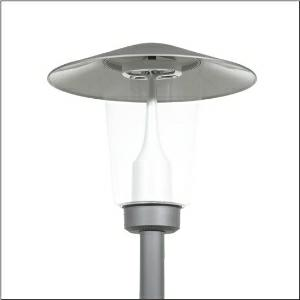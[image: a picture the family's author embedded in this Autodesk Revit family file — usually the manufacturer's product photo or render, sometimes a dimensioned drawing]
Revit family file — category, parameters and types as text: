
# Revit family: pilzleuchte_iq___p1_0a_5xa5235bf14hp_6096
name_source: partatom
category: Lighting Fixtures
units: mm (PartAtom-declared; Revit-internal decimal feet)

## family parameters
Cut with Voids When Loaded = No
Host = Face
Light Source = No
Part Type = Normal
Room Calculation Point = No
Round Connector Dimension = Use Diameter
Shared = No

## types (1)
- --- (1 x LED, 3920 lm, 33.6 W, 2200K)
    Apparent Load = 34 VA
    CIE Flux Codes = 35 64 90 96 100
    Color Rendering = 70
    Color Temperature = 2200K
    Default Elevation = 1800 mm
    Description = Mushroom Luminaire iQ, mast luminaire, Module 540 iQ-SR, primary light control with 3 zone facetted reflector, of plastic, silver coated, highly specular, structured, primary optical cover: cover, of PMMA, transparent, light distribution: P1.0a, light emission: direct distribution, primary light characteristic: strongly asymmetric, installation type: post-top, LED, High Power LED, rated luminous flux: 3.920lm, luminous efficacy: 117lm/W, light colour: 722, colour temperature: 2200K, control gear: iQ Street-Remote, control: pre-setting: logarithmic dimming characteristic, Street-Remote, Auto-Match, Temp-Guard, Lumen-Switch, Night-Set, Smart-Wire, Light-Fading, Desk-Remote (wireless, voltage-free reading and setting of iQ features in the workshop via application-optimized NFC function/RFID function), optimised constant luminous flux control (CLO 2.0), with terminal, 6-pole, max. 2.5mm², mains connection: 230..240V, AC, 50/60Hz, start of lifetime: 34W, end of service life: 36W, reduction: 15W, luminaire housing, upper part, of glass-fibre reinforced polyester, coated, Siteco® metallic grey (DB 702S), diameter: 650mm, height: 586mm, spigot size: d x l = 76 x 70mm (post-top) | with reducer (optional accessory) 60 x 70mm, mounting height: 3..5m, post-top mast mounting element, of diecast aluminium, coated, Siteco® metallic grey (DB 702S), Module 540 iQ-SR, traffic white (RAL 9016), equipment: Power, protection rating (complete): IP65, insulation class (complete): insulation class II (safety insulation), certification: CE, ENEC, VDE, packaging unit: 1 piece

Light Distribution: P1.0a
    Height = 586 mm
    Lamp = 1 x LED
    Lamp Light Flux = 3920 lm
    Lamp Power = 33.6 W
    Lamp count = 1
    Length = 650 mm
    Luminous efficacy = 117 lm/W
    Manufacturer = Siteco
    ModVariant = No
    Model = 5XA5235BF14HP
    Number of Poles = 1
    OnlyDefault = Yes
    Power Factor = 1
    Product Name = Pilzleuchte iQ | P1.0a
    Product group = mast luminaire | pylon top
    ProductGroupID = 6100
    Protection Class = Protection class II
    Protection Degree = IP 65
    RLX_Detail_Level = 1
    RLX_Emergency_Light_Flux = 0 lm
    RLX_Emergency_Type = 0
    RLX_Emergency_Type_DB = No
    RlxData = <blob elided: 52005 chars, md5=1ad8eb23>
    Socket = socket
    Standby Power = 0 W
    System Light Flux = 3920 lm
    System Power = 34 W
    Type Comments = factory setting: luminous flux: 100 % | dim-lin: 254 | 695 mA
    Type Image = l_1006077.jpg
    URL = http://relux.com
    VarID = @adj_213483
    Voltage = 0 V
    Weight = 0.00 kg
    Width = 0 mm  [stored 0 ft]

note: [stored X ft] marks values corroborated as IEEE doubles in the binary element streams (Revit-internal decimal feet)

## geometry (parser evidence)
native form markers: Blend x4, Sweep x11
no freeform markers — native parametric forms only
